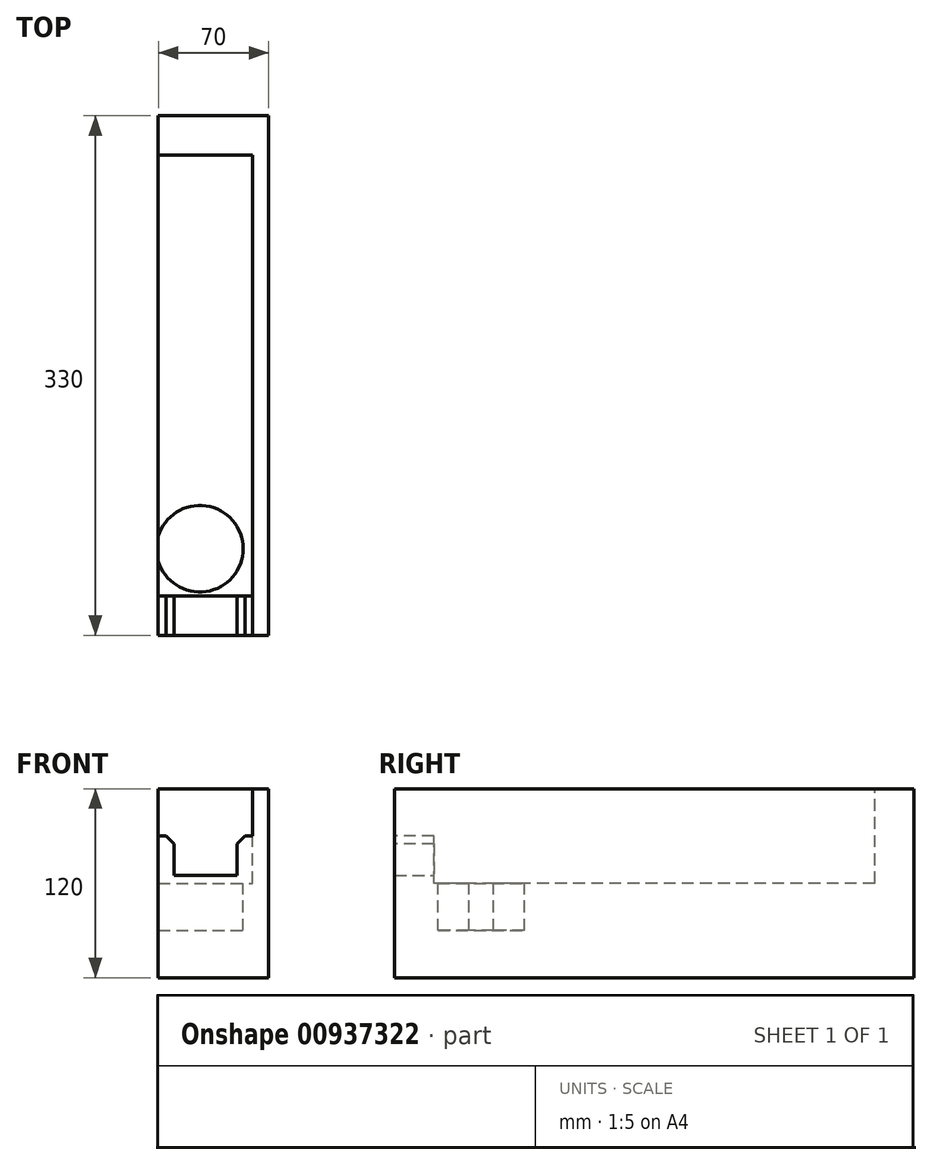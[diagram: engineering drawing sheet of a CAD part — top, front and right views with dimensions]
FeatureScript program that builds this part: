
annotation { "Feature Type Name" : "Feature", "Feature Type Description" : "" }
export const myFeature = defineFeature(function(context is Context, id is Id, definition is map)
    precondition{}
    {
        {
            var Q0;
            Q0=qCreatedBy(makeId("Top.planeOp"),FACE);
            var sketch = newSketch(context, id + "F0", { "sketchPlane" : qUnion([Q0])});
            skLineSegment(sketch, "E0.bottom", {"start": v(-35.98, 200.84) * mm, "end": v(34.02, 200.84) * mm});
            skLineSegment(sketch, "E0.top", {"start": v(-35.98, -129.16) * mm, "end": v(34.02, -129.16) * mm});
            skLineSegment(sketch, "E0.left", {"start": v(-35.98, 200.84) * mm, "end": v(-35.98, -129.16) * mm});
            skLineSegment(sketch, "E0.right", {"start": v(34.02, 200.84) * mm, "end": v(34.02, -129.16) * mm});
            skSolve(sketch);
        }
        {
            var Q0;
            Q0 = qSketchRegion(id + "F0", true);
            extrude(context, id + "F1", {"entities" : qUnion([Q0]), "depth" : 120 * mm, "offsetDistance" : 25 * mm});
        }
        {
            var Q0;
            Q0=makeQuery(id+"F1.opExtrude","CAP_FACE",FACE,{"disambiguationData":[OSD([sQuery(id+"F0.wireOp",EDGE,"E0.bottom"),sQuery(id+"F0.wireOp",EDGE,"E0.top"),sQuery(id+"F0.wireOp",EDGE,"E0.left"),sQuery(id+"F0.wireOp",EDGE,"E0.right")])],"isStart":false});
            var sketch = newSketch(context, id + "F2", { "sketchPlane" : qUnion([Q0])});
            skLineSegment(sketch, "E1.bottom", {"start": v(-35.98, 175.84) * mm, "end": v(24.02, 175.84) * mm});
            skLineSegment(sketch, "E1.top", {"start": v(-35.98, -104.16) * mm, "end": v(24.02, -104.16) * mm});
            skLineSegment(sketch, "E1.left", {"start": v(-35.98, 175.84) * mm, "end": v(-35.98, -104.16) * mm});
            skLineSegment(sketch, "E1.right", {"start": v(24.02, 175.84) * mm, "end": v(24.02, -104.16) * mm});
            skSolve(sketch);
        }
        {
            var Q0;
            Q0=makeQuery(id+"F2.imprint","IMPRINT",FACE,{"disambiguationData":[TD([[makeQuery(id+"F2.imprint","IMPRINT",EDGE,{"derivedFrom":sQuery(id+"F2.wireOp",EDGE,"E1.bottom")}),-1.0]])]});
            extrude(context, id + "F3", {"entities" : qUnion([Q0]), "operationType" : NewBodyOperationType.REMOVE, "oppositeDirection" : true, "depth" : 60 * mm, "offsetDistance" : 25 * mm});
        }
        {
            var Q0;
            Q0=makeQuery(id+"F3.boolean.opBoolean","COPY",FACE,{"derivedFrom":makeQuery(id+"F3.opExtrude","CAP_FACE",FACE,{"disambiguationData":[OSD([sQuery(id+"F2.wireOp",EDGE,"E1.bottom"),sQuery(id+"F2.wireOp",EDGE,"E1.top"),sQuery(id+"F2.wireOp",EDGE,"E1.left"),sQuery(id+"F2.wireOp",EDGE,"E1.right")])],"isStart":false})});
            var sketch = newSketch(context, id + "F4", { "sketchPlane" : qUnion([Q0])});
            skCircle(sketch, "E2", {"center": v(-9.62, -74.16) * mm, "radius": 27.5 * mm});
            skSolve(sketch);
        }
        {
            var Q0;
            Q0 = qSketchRegion(id + "F4", true);
            extrude(context, id + "F5", {"entities" : qUnion([Q0]), "operationType" : NewBodyOperationType.REMOVE, "oppositeDirection" : true, "depth" : 30 * mm, "offsetDistance" : 25 * mm});
        }
        {
            var Q0;
            Q0=makeQuery(id+"F1.opExtrude","SWEPT_FACE",FACE,{"disambiguationData":[OSD([sQuery(id+"F0.wireOp",EDGE,"E0.top")])]});
            var sketch = newSketch(context, id + "F6", { "sketchPlane" : qUnion([Q0])});
            skLineSegment(sketch, "E3.bottom", {"start": v(-35.98, 120) * mm, "end": v(24.02, 120) * mm});
            skLineSegment(sketch, "E3.top", {"start": v(-35.98, 65) * mm, "end": v(24.02, 65) * mm});
            skLineSegment(sketch, "E3.left", {"start": v(-35.98, 120) * mm, "end": v(-35.98, 65) * mm});
            skLineSegment(sketch, "E3.right", {"start": v(24.02, 120) * mm, "end": v(24.02, 65) * mm});
            skSolve(sketch);
        }
        {
            var Q0;
            Q0=makeQuery(id+"F6.imprint","IMPRINT",FACE,{"disambiguationData":[TD([[makeQuery(id+"F6.imprint","IMPRINT",EDGE,{"derivedFrom":sQuery(id+"F6.wireOp",EDGE,"E3.bottom")}),-1.0]])]});
            extrude(context, id + "F7", {"entities" : qUnion([Q0]), "operationType" : NewBodyOperationType.REMOVE, "endBound" : BoundingType.UP_TO_NEXT, "oppositeDirection" : true, "depth" : 25 * mm, "offsetDistance" : 25 * mm});
        }
        {
            var Q0;
            Q0=makeQuery(id+"F7.boolean.opBoolean","COPY",FACE,{"derivedFrom":makeQuery(id+"F7.opExtrude","SWEPT_FACE",FACE,{"disambiguationData":[OSD([sQuery(id+"F6.wireOp",EDGE,"E3.top")])]})});
            var sketch = newSketch(context, id + "F8", { "sketchPlane" : qUnion([Q0])});
            skLineSegment(sketch, "E4.bottom", {"start": v(-35.98, -104.16) * mm, "end": v(-25.98, -104.16) * mm});
            skLineSegment(sketch, "E4.top", {"start": v(-35.98, -129.16) * mm, "end": v(-25.98, -129.16) * mm});
            skLineSegment(sketch, "E4.left", {"start": v(-35.98, -104.16) * mm, "end": v(-35.98, -129.16) * mm});
            skLineSegment(sketch, "E4.right", {"start": v(-25.98, -104.16) * mm, "end": v(-25.98, -129.16) * mm});
            skLineSegment(sketch, "E5.bottom", {"start": v(24.02, -129.16) * mm, "end": v(14.02, -129.16) * mm});
            skLineSegment(sketch, "E5.top", {"start": v(24.02, -104.16) * mm, "end": v(14.02, -104.16) * mm});
            skLineSegment(sketch, "E5.left", {"start": v(24.02, -129.16) * mm, "end": v(24.02, -104.16) * mm});
            skLineSegment(sketch, "E5.right", {"start": v(14.02, -129.16) * mm, "end": v(14.02, -104.16) * mm});
            skSolve(sketch);
        }
        {
            var Q0;
            Q0=makeQuery(id+"F8.imprint","IMPRINT",FACE,{"disambiguationData":[TD([[makeQuery(id+"F8.imprint","IMPRINT",EDGE,{"derivedFrom":sQuery(id+"F8.wireOp",EDGE,"E4.bottom")}),1.0]])]});
            extrude(context, id + "F9", {"entities" : qUnion([Q0]), "operationType" : NewBodyOperationType.ADD, "depth" : 25 * mm, "offsetDistance" : 25 * mm});
        }
        {
            var Q0;
            Q0=makeQuery(id+"F8.imprint","IMPRINT",FACE,{"disambiguationData":[TD([[makeQuery(id+"F8.imprint","IMPRINT",EDGE,{"derivedFrom":sQuery(id+"F8.wireOp",EDGE,"E5.bottom")}),1.0]])]});
            extrude(context, id + "F10", {"entities" : qUnion([Q0]), "operationType" : NewBodyOperationType.ADD, "depth" : 25 * mm, "offsetDistance" : 25 * mm});
        }
        {
            var Q0;
            Q0=makeQuery(id+"F10.opExtrude","CAP_EDGE",EDGE,{"disambiguationData":[OSD([sQuery(id+"F8.wireOp",EDGE,"E5.right")])],"isStart":false});
            chamfer(context, id + "F11", {"entities" : qUnion([Q0]), "width" : 5 * mm, "tangentPropagation" : true});
        }
        {
            var Q0;
            Q0=makeQuery(id+"F9.opExtrude","CAP_EDGE",EDGE,{"disambiguationData":[OSD([sQuery(id+"F8.wireOp",EDGE,"E4.right")])],"isStart":false});
            chamfer(context, id + "F12", {"entities" : qUnion([Q0]), "width" : 5 * mm, "tangentPropagation" : true});
        }
    });
